# Revit family: BC_Hitachi_RAS2-2.5-HVNP1_LOD200
name_source: partatom
category: Equipement de génie climatique
revit_build: Autodesk Revit 2016 (Build: 20150220_1215(x64)
units: mm (PartAtom-declared; Revit-internal decimal feet)

## family parameters
Basée sur le plan de construction = Non
Cote de connecteur circulaire = Utiliser le diamètre
Couper avec des vides une fois chargée = Non
Numéro OmniClass = 23.75.00.00
Partagée = Non
Point de calcul de pièce = Non
Titre OmniClass = Climate Control (HVAC)
Toujours verticalement = Oui
Type d'élément = Normal

## types (2) — shared parameters
Commentaires du type = RAS HVNP
Description = The CENTRIFUGE IVX solution has been created for integrate this outdoor group inside the building
Fabricant = HITACHI
Fan diameter = 500.00 mm
Frequency = 50 Hz
Gas Diameter = 12.70 mm
Heating Capacity = 6 kW
Height Gas pipe = 172.00 mm
Height Liquid pipe = 111.00 mm
Liquid Diameter = 6.35 mm
Mass = 41.00 kg
Maximum AC Voltage = 253 V
Maximum Air Flow = 40600.0 L/min
Maximum Connected Capacity (%) = 110
Minimum AC Voltage = 207 V
Minimum Connected Capacity (%) = 90
Modèle = Outdoor Unit - IVX Premium
Nominal Voltage = 230 V
Nominal cooling capacity (max) = 6 kW
Nominal cooling capacity (min) = 2 kW
Nominal cooling power input = 1 kW
Nominal heating capacity (min) = 2 kW
Nominal heating power input = 1 kW
Number of Poles = 1
Overall Depth = 300.00 mm
Overall Height = 600.00 mm
Overall Width = 792.00 mm
Refrigerant = R410A
Refrigerant charge = 1.60 kg

## per-type parameters (varying)
| type | Coefficient Of Performance (COP) | Cooling Capacity | Energy Efficiency Ratio (EER) | Maximum Input Power | Nominal Current | Nominal heating capacity (max) | Product Code | Recommended circuit breaker | Running current cooling | Running current heating | Sound power at rated load (dB(A)) | Sound pressure level Night mode cooling (dB(A)) | Sound pressure level cooling (dB(A)) | Sound pressure level heating (dB(A)) |
| RAS-2HVNP1 | 4.68 | 5 kW | 4.03 | 3 kW | 12 A | 7 kW | 60288615 | 16 A | 5 A | 5 A | 62 | 42 | 44 | 49 |
| RAS-2.5HVNP1 | 4.92 | 6 kW | 4.18 | 4 kW | 14 A | 8 kW | 60288616 | 20 A | 6 A | 6 A | 63 | 43 | 45 | 47 |

## geometry (parser evidence)
native form markers: Blend x2
no freeform markers — native parametric forms only
